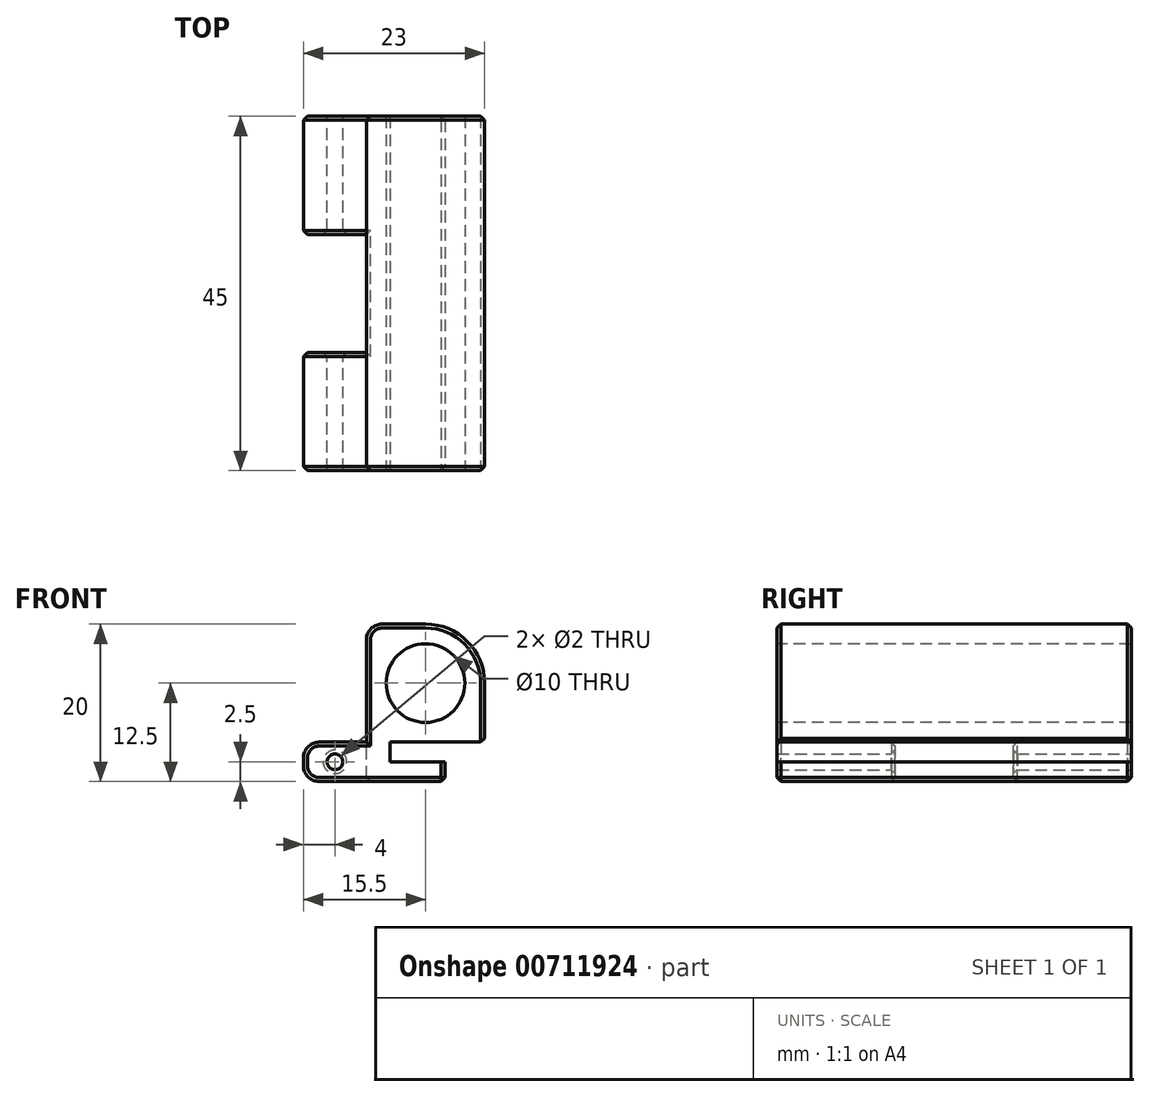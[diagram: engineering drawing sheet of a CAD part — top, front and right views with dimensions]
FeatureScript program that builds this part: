
annotation { "Feature Type Name" : "Feature", "Feature Type Description" : "" }
export const myFeature = defineFeature(function(context is Context, id is Id, definition is map)
    precondition{}
    {
        {
            var Q0;
            Q0=qCreatedBy(makeId("Front.planeOp"),FACE);
            var sketch = newSketch(context, id + "F0", { "sketchPlane" : qUnion([Q0])});
            skLineSegment(sketch, "E0.bottom", {"start": v(0, 0) * mm, "end": v(15, 0) * mm});
            skLineSegment(sketch, "E0.top", {"start": v(0, 15) * mm, "end": v(15, 15) * mm});
            skLineSegment(sketch, "E0.left", {"start": v(0, 0) * mm, "end": v(0, 15) * mm});
            skLineSegment(sketch, "E0.right", {"start": v(15, 0) * mm, "end": v(15, 15) * mm});
            skSolve(sketch);
        }
        {
            var Q0;
            Q0=makeQuery(id+"F0.imprint","IMPRINT",FACE,{"disambiguationData":[TD([[makeQuery(id+"F0.imprint","IMPRINT",EDGE,{"derivedFrom":sQuery(id+"F0.wireOp",EDGE,"E0.bottom")}),1.0]])]});
            extrude(context, id + "F1", {"entities" : qUnion([Q0]), "oppositeDirection" : true, "depth" : 45 * mm, "offsetDistance" : 25 * mm});
        }
        {
            var Q0;
            Q0=makeQuery(id+"F1.opExtrude","CAP_FACE",FACE,{"disambiguationData":[OSD([sQuery(id+"F0.wireOp",EDGE,"E0.bottom"),sQuery(id+"F0.wireOp",EDGE,"E0.top"),sQuery(id+"F0.wireOp",EDGE,"E0.left"),sQuery(id+"F0.wireOp",EDGE,"E0.right")])],"isStart":true});
            var sketch = newSketch(context, id + "F2", { "sketchPlane" : qUnion([Q0])});
            skCircle(sketch, "E1", {"center": v(7.5, 7.5) * mm, "radius": 5 * mm});
            skPoint(sketch, "E1.centerSnap0", {"position": v(15, 7.5) * mm});
            skPoint(sketch, "E1.centerSnap1", {"position": v(7.5, 0) * mm});
            skSolve(sketch);
        }
        {
            var Q0;
            Q0 = qSketchRegion(id + "F2", true);
            extrude(context, id + "F3", {"entities" : qUnion([Q0]), "operationType" : NewBodyOperationType.REMOVE, "oppositeDirection" : true, "depth" : 45 * mm, "offsetDistance" : 25 * mm});
        }
        {
            var Q0;
            Q0=makeQuery(id+"F1.opExtrude","SWEPT_EDGE",EDGE,{"disambiguationData":[OSD([sQuery(id+"F0.wireOp",EDGE,"E0.top"),sQuery(id+"F0.wireOp",EDGE,"E0.right")])]});
            fillet(context, id + "F4", {"entities" : qUnion([Q0]), "tangentPropagation" : true, "radius" : 7.5 * mm, "defaultsChanged" : false, "vertexSettings" : [], "allowEdgeOverflow" : false});
        }
        {
            var Q0;
            Q0=makeQuery(id+"F1.opExtrude","SWEPT_FACE",FACE,{"disambiguationData":[OSD([sQuery(id+"F0.wireOp",EDGE,"E0.left")])]});
            var sketch = newSketch(context, id + "F5", { "sketchPlane" : qUnion([Q0])});
            skSolve(sketch);
        }
        {
            var Q0;
            Q0=makeQuery(id+"F1.opExtrude","CAP_FACE",FACE,{"disambiguationData":[OSD([sQuery(id+"F0.wireOp",EDGE,"E0.bottom"),sQuery(id+"F0.wireOp",EDGE,"E0.top"),sQuery(id+"F0.wireOp",EDGE,"E0.left"),sQuery(id+"F0.wireOp",EDGE,"E0.right")])],"isStart":true});
            var sketch = newSketch(context, id + "F6", { "sketchPlane" : qUnion([Q0])});
            skLineSegment(sketch, "E2.bottom", {"start": v(0, 0) * mm, "end": v(10, 0) * mm});
            skLineSegment(sketch, "E2.top", {"start": v(0, -5) * mm, "end": v(10, -5) * mm});
            skLineSegment(sketch, "E2.left", {"start": v(0, 0) * mm, "end": v(0, -5) * mm});
            skLineSegment(sketch, "E2.right", {"start": v(10, 0) * mm, "end": v(10, -5) * mm});
            skSolve(sketch);
        }
        {
            var Q0;
            Q0 = qSketchRegion(id + "F6", true);
            extrude(context, id + "F7", {"entities" : qUnion([Q0]), "operationType" : NewBodyOperationType.ADD, "oppositeDirection" : true, "depth" : 45 * mm, "offsetDistance" : 25 * mm});
        }
        {
            var Q0;
            Q0=makeQuery(id+"F7.boolean.opBoolean","MERGE",FACE,{"derivedFrom":[makeQuery(id+"F1.opExtrude","CAP_FACE",FACE,{"disambiguationData":[OSD([sQuery(id+"F0.wireOp",EDGE,"E0.bottom"),sQuery(id+"F0.wireOp",EDGE,"E0.top"),sQuery(id+"F0.wireOp",EDGE,"E0.left"),sQuery(id+"F0.wireOp",EDGE,"E0.right")])],"isStart":true}),makeQuery(id+"F7.opExtrude","CAP_FACE",FACE,{"disambiguationData":[OSD([sQuery(id+"F6.wireOp",EDGE,"E2.bottom"),sQuery(id+"F6.wireOp",EDGE,"E2.top"),sQuery(id+"F6.wireOp",EDGE,"E2.left"),sQuery(id+"F6.wireOp",EDGE,"E2.right")])],"isStart":true})]});
            var sketch = newSketch(context, id + "F8", { "sketchPlane" : qUnion([Q0])});
            skPoint(sketch, "E3.oppositeSnap0", {"position": v(10, -2.5) * mm});
            skLineSegment(sketch, "E3.bottom", {"start": v(10, 0) * mm, "end": v(3, 0) * mm});
            skLineSegment(sketch, "E3.top", {"start": v(10, -2.5) * mm, "end": v(3, -2.5) * mm});
            skLineSegment(sketch, "E3.left", {"start": v(10, 0) * mm, "end": v(10, -2.5) * mm});
            skLineSegment(sketch, "E3.right", {"start": v(3, 0) * mm, "end": v(3, -2.5) * mm});
            skSolve(sketch);
        }
        {
            var Q0;
            Q0 = qSketchRegion(id + "F8", true);
            extrude(context, id + "F9", {"entities" : qUnion([Q0]), "operationType" : NewBodyOperationType.REMOVE, "oppositeDirection" : true, "depth" : 45 * mm, "offsetDistance" : 25 * mm});
        }
        {
            var Q0;
            {var subQ0=sQuery(id+"F0.wireOp",EDGE,"E0.left");Q0=makeQuery(id+"F5.imprint","IMPRINT",FACE,{"disambiguationData":[TD([[makeQuery(id+"F5.imprint","IMPRINT",EDGE,{"derivedFrom":makeQuery(id+"F1.opExtrude","CAP_EDGE",EDGE,{"disambiguationData":[OSD([subQ0])],"isStart":true})}),1.0]])]});}
            var sketch = newSketch(context, id + "F10", { "sketchPlane" : qUnion([Q0])});
            skLineSegment(sketch, "E4.bottom", {"start": v(0, 0) * mm, "end": v(-15, 0) * mm});
            skLineSegment(sketch, "E4.top", {"start": v(0, -5) * mm, "end": v(-15, -5) * mm});
            skLineSegment(sketch, "E4.left", {"start": v(0, 0) * mm, "end": v(0, -5) * mm});
            skLineSegment(sketch, "E4.right", {"start": v(-15, 0) * mm, "end": v(-15, -5) * mm});
            skSolve(sketch);
        }
        {
            var Q0;
            Q0 = qSketchRegion(id + "F10", true);
            extrude(context, id + "F11", {"entities" : qUnion([Q0]), "operationType" : NewBodyOperationType.ADD, "depth" : 8 * mm, "offsetDistance" : 25 * mm});
        }
        {
            var Q0;
            Q0=makeQuery(id+"F7.boolean.opBoolean","MERGE",FACE,{"derivedFrom":[makeQuery(id+"F1.opExtrude","SWEPT_FACE",FACE,{"disambiguationData":[OSD([sQuery(id+"F0.wireOp",EDGE,"E0.left")])]}),makeQuery(id+"F7.opExtrude","SWEPT_FACE",FACE,{"disambiguationData":[OSD([sQuery(id+"F6.wireOp",EDGE,"E2.left")])]})]});
            var sketch = newSketch(context, id + "F12", { "sketchPlane" : qUnion([Q0])});
            skLineSegment(sketch, "E5.bottom", {"start": v(-45, -5) * mm, "end": v(-30, -5) * mm});
            skLineSegment(sketch, "E5.top", {"start": v(-45, 0) * mm, "end": v(-30, 0) * mm});
            skLineSegment(sketch, "E5.left", {"start": v(-45, -5) * mm, "end": v(-45, 0) * mm});
            skLineSegment(sketch, "E5.right", {"start": v(-30, -5) * mm, "end": v(-30, 0) * mm});
            skSolve(sketch);
        }
        {
            var Q0;
            Q0 = qSketchRegion(id + "F12", true);
            extrude(context, id + "F13", {"entities" : qUnion([Q0]), "operationType" : NewBodyOperationType.ADD, "depth" : 8 * mm, "offsetDistance" : 25 * mm});
        }
        {
            var Q0;
            Q0=makeQuery(id+"F13.boolean.opBoolean","MERGE",FACE,{"derivedFrom":[makeQuery(id+"F7.boolean.opBoolean","MERGE",FACE,{"derivedFrom":[makeQuery(id+"F1.opExtrude","CAP_FACE",FACE,{"disambiguationData":[OSD([sQuery(id+"F0.wireOp",EDGE,"E0.bottom"),sQuery(id+"F0.wireOp",EDGE,"E0.top"),sQuery(id+"F0.wireOp",EDGE,"E0.left"),sQuery(id+"F0.wireOp",EDGE,"E0.right")])],"isStart":false}),makeQuery(id+"F7.opExtrude","CAP_FACE",FACE,{"disambiguationData":[OSD([sQuery(id+"F6.wireOp",EDGE,"E2.bottom"),sQuery(id+"F6.wireOp",EDGE,"E2.top"),sQuery(id+"F6.wireOp",EDGE,"E2.left"),sQuery(id+"F6.wireOp",EDGE,"E2.right")])],"isStart":false})]}),makeQuery(id+"F13.opExtrude","SWEPT_FACE",FACE,{"disambiguationData":[OSD([sQuery(id+"F12.wireOp",EDGE,"E5.left")])]})]});
            var sketch = newSketch(context, id + "F14", { "sketchPlane" : qUnion([Q0])});
            skCircle(sketch, "E6", {"center": v(4, -2.5) * mm, "radius": 1 * mm});
            skPoint(sketch, "E6.centerSnap0", {"position": v(4, 0) * mm});
            skPoint(sketch, "E6.centerSnap1", {"position": v(8, -2.5) * mm});
            skSolve(sketch);
        }
        {
            var Q0;
            Q0 = qSketchRegion(id + "F14", true);
            extrude(context, id + "F15", {"entities" : qUnion([Q0]), "operationType" : NewBodyOperationType.REMOVE, "oppositeDirection" : true, "depth" : 45 * mm, "offsetDistance" : 25 * mm});
        }
        {
            var Q0;
            Q0=makeQuery(id+"F13.opExtrude","CAP_EDGE",EDGE,{"disambiguationData":[OSD([sQuery(id+"F12.wireOp",EDGE,"E5.top")])],"isStart":false});
            var Q1;
            Q1=makeQuery(id+"F13.opExtrude","CAP_EDGE",EDGE,{"disambiguationData":[OSD([sQuery(id+"F12.wireOp",EDGE,"E5.bottom")])],"isStart":false});
            var Q2;
            Q2=makeQuery(id+"F11.opExtrude","CAP_EDGE",EDGE,{"disambiguationData":[OSD([sQuery(id+"F10.wireOp",EDGE,"E4.top")])],"isStart":false});
            var Q3;
            Q3=makeQuery(id+"F11.opExtrude","CAP_EDGE",EDGE,{"disambiguationData":[OSD([sQuery(id+"F10.wireOp",EDGE,"E4.bottom")])],"isStart":false});
            var Q4;
            Q4=makeQuery(id+"F1.opExtrude","SWEPT_EDGE",EDGE,{"disambiguationData":[OSD([sQuery(id+"F0.wireOp",EDGE,"E0.top"),sQuery(id+"F0.wireOp",EDGE,"E0.left")])]});
            fillet(context, id + "F16", {"entities" : qUnion([Q0, Q1, Q2, Q3, Q4]), "tangentPropagation" : true, "radius" : 2 * mm, "defaultsChanged" : false, "vertexSettings" : [], "allowEdgeOverflow" : false});
        }
        {
            var Q0;
            Q0=makeQuery(id+"F7.boolean.opBoolean","MERGE",EDGE,{"derivedFrom":[makeQuery(id+"F1.opExtrude","CAP_EDGE",EDGE,{"disambiguationData":[OSD([sQuery(id+"F0.wireOp",EDGE,"E0.left")])],"isStart":true}),makeQuery(id+"F7.opExtrude","CAP_EDGE",EDGE,{"disambiguationData":[OSD([sQuery(id+"F6.wireOp",EDGE,"E2.left")])],"isStart":true})]});
            var Q1;
            Q1=makeQuery(id+"F11.opExtrude","SWEPT_EDGE",EDGE,{"disambiguationData":[OSD([sQuery(id+"F0.wireOp",EDGE,"E0.left"),sQuery(id+"F10.wireOp",EDGE,"E4.bottom"),sQuery(id+"F10.wireOp",EDGE,"E4.left")])]});
            var Q2;
            Q2=makeQuery(id+"F7.opExtrude","CAP_EDGE",EDGE,{"disambiguationData":[OSD([sQuery(id+"F6.wireOp",EDGE,"E2.right")])],"isStart":true});
            var Q3;
            Q3=makeQuery(id+"F9.boolean.opBoolean","COPY",EDGE,{"derivedFrom":makeQuery(id+"F9.opExtrude","CAP_EDGE",EDGE,{"disambiguationData":[OSD([sQuery(id+"F8.wireOp",EDGE,"E3.top")])],"isStart":true})});
            var Q4;
            Q4=makeQuery(id+"F9.boolean.opBoolean","COPY",EDGE,{"derivedFrom":makeQuery(id+"F9.opExtrude","CAP_EDGE",EDGE,{"disambiguationData":[OSD([sQuery(id+"F8.wireOp",EDGE,"E3.right")])],"isStart":true})});
            var Q5;
            Q5=makeQuery(id+"F9.boolean.opBoolean","MERGE",EDGE,{"derivedFrom":[makeQuery(id+"F1.opExtrude","CAP_EDGE",EDGE,{"disambiguationData":[OSD([sQuery(id+"F0.wireOp",EDGE,"E0.bottom")])],"isStart":true})],"fromTools":[makeQuery(id+"F9.opExtrude","CAP_EDGE",EDGE,{"disambiguationData":[OSD([sQuery(id+"F8.wireOp",EDGE,"E3.bottom")])],"isStart":true})]});
            var Q6;
            Q6=makeQuery(id+"F3.boolean.opBoolean","COPY",EDGE,{"derivedFrom":makeQuery(id+"F3.opExtrude","CAP_EDGE",EDGE,{"disambiguationData":[OSD([sQuery(id+"F2.wireOp",EDGE,"E1")])],"isStart":true})});
            var Q7;
            Q7=makeQuery(id+"F11.opExtrude","SWEPT_EDGE",EDGE,{"disambiguationData":[OSD([sQuery(id+"F10.wireOp",EDGE,"E4.top"),sQuery(id+"F10.wireOp",EDGE,"E4.right")])]});
            var Q8;
            Q8=makeQuery(id+"F15.boolean.opBoolean","INTERSECT",EDGE,{"derivedFrom":[makeQuery(id+"F11.opExtrude","SWEPT_FACE",FACE,{"disambiguationData":[OSD([sQuery(id+"F10.wireOp",EDGE,"E4.right")])]}),makeQuery(id+"F15.opExtrude","SWEPT_FACE",FACE,{"disambiguationData":[OSD([sQuery(id+"F14.wireOp",EDGE,"E6")])]})]});
            var Q9;
            Q9=makeQuery(id+"F15.boolean.opBoolean","COPY",EDGE,{"derivedFrom":makeQuery(id+"F15.opExtrude","CAP_EDGE",EDGE,{"disambiguationData":[OSD([sQuery(id+"F14.wireOp",EDGE,"E6")])],"isStart":false})});
            var Q10;
            Q10=makeQuery(id+"F15.boolean.opBoolean","INTERSECT",EDGE,{"derivedFrom":[makeQuery(id+"F13.opExtrude","SWEPT_FACE",FACE,{"disambiguationData":[OSD([sQuery(id+"F12.wireOp",EDGE,"E5.right")])]}),makeQuery(id+"F15.opExtrude","SWEPT_FACE",FACE,{"disambiguationData":[OSD([sQuery(id+"F14.wireOp",EDGE,"E6")])]})]});
            var Q11;
            Q11=makeQuery(id+"F13.opExtrude","SWEPT_EDGE",EDGE,{"disambiguationData":[OSD([sQuery(id+"F6.wireOp",EDGE,"E2.top"),sQuery(id+"F6.wireOp",EDGE,"E2.left"),sQuery(id+"F12.wireOp",EDGE,"E5.bottom"),sQuery(id+"F12.wireOp",EDGE,"E5.right")])]});
            var Q12;
            Q12=makeQuery(id+"F16.opFillet","BLEND_EDGE",EDGE,{"blendedFrom":[makeQuery(id+"F13.opExtrude","CAP_EDGE",EDGE,{"disambiguationData":[OSD([sQuery(id+"F12.wireOp",EDGE,"E5.bottom")])],"isStart":false}),makeQuery(id+"F13.boolean.opBoolean","MERGE",FACE,{"derivedFrom":[makeQuery(id+"F7.boolean.opBoolean","MERGE",FACE,{"derivedFrom":[makeQuery(id+"F1.opExtrude","CAP_FACE",FACE,{"disambiguationData":[OSD([sQuery(id+"F0.wireOp",EDGE,"E0.bottom"),sQuery(id+"F0.wireOp",EDGE,"E0.top"),sQuery(id+"F0.wireOp",EDGE,"E0.left"),sQuery(id+"F0.wireOp",EDGE,"E0.right")])],"isStart":false}),makeQuery(id+"F7.opExtrude","CAP_FACE",FACE,{"disambiguationData":[OSD([sQuery(id+"F6.wireOp",EDGE,"E2.bottom"),sQuery(id+"F6.wireOp",EDGE,"E2.top"),sQuery(id+"F6.wireOp",EDGE,"E2.left"),sQuery(id+"F6.wireOp",EDGE,"E2.right")])],"isStart":false})]}),makeQuery(id+"F13.opExtrude","SWEPT_FACE",FACE,{"disambiguationData":[OSD([sQuery(id+"F12.wireOp",EDGE,"E5.left")])]})]})],"blendedInto":[makeQuery(id+"F13.boolean.opBoolean","MERGE",FACE,{"derivedFrom":[makeQuery(id+"F7.boolean.opBoolean","MERGE",FACE,{"derivedFrom":[makeQuery(id+"F1.opExtrude","CAP_FACE",FACE,{"disambiguationData":[OSD([sQuery(id+"F0.wireOp",EDGE,"E0.bottom"),sQuery(id+"F0.wireOp",EDGE,"E0.top"),sQuery(id+"F0.wireOp",EDGE,"E0.left"),sQuery(id+"F0.wireOp",EDGE,"E0.right")])],"isStart":false}),makeQuery(id+"F7.opExtrude","CAP_FACE",FACE,{"disambiguationData":[OSD([sQuery(id+"F6.wireOp",EDGE,"E2.bottom"),sQuery(id+"F6.wireOp",EDGE,"E2.top"),sQuery(id+"F6.wireOp",EDGE,"E2.left"),sQuery(id+"F6.wireOp",EDGE,"E2.right")])],"isStart":false})]}),makeQuery(id+"F13.opExtrude","SWEPT_FACE",FACE,{"disambiguationData":[OSD([sQuery(id+"F12.wireOp",EDGE,"E5.left")])]})]})]});
            var Q13;
            Q13=makeQuery(id+"F7.opExtrude","CAP_EDGE",EDGE,{"disambiguationData":[OSD([sQuery(id+"F6.wireOp",EDGE,"E2.right")])],"isStart":false});
            var Q14;
            Q14=makeQuery(id+"F9.boolean.opBoolean","COPY",EDGE,{"derivedFrom":makeQuery(id+"F9.opExtrude","CAP_EDGE",EDGE,{"disambiguationData":[OSD([sQuery(id+"F8.wireOp",EDGE,"E3.top")])],"isStart":false})});
            var Q15;
            Q15=makeQuery(id+"F9.boolean.opBoolean","COPY",EDGE,{"derivedFrom":makeQuery(id+"F9.opExtrude","CAP_EDGE",EDGE,{"disambiguationData":[OSD([sQuery(id+"F8.wireOp",EDGE,"E3.right")])],"isStart":false})});
            var Q16;
            Q16=makeQuery(id+"F9.boolean.opBoolean","MERGE",EDGE,{"derivedFrom":[makeQuery(id+"F1.opExtrude","CAP_EDGE",EDGE,{"disambiguationData":[OSD([sQuery(id+"F0.wireOp",EDGE,"E0.bottom")])],"isStart":false})],"fromTools":[makeQuery(id+"F9.opExtrude","CAP_EDGE",EDGE,{"disambiguationData":[OSD([sQuery(id+"F8.wireOp",EDGE,"E3.bottom")])],"isStart":false})]});
            var Q17;
            Q17=makeQuery(id+"F3.boolean.opBoolean","COPY",EDGE,{"derivedFrom":makeQuery(id+"F3.opExtrude","CAP_EDGE",EDGE,{"disambiguationData":[OSD([sQuery(id+"F2.wireOp",EDGE,"E1")])],"isStart":false})});
            var Q18;
            Q18=makeQuery(id+"F1.opExtrude","CAP_EDGE",EDGE,{"disambiguationData":[OSD([sQuery(id+"F0.wireOp",EDGE,"E0.right")])],"isStart":false});
            var Q19;
            Q19=makeQuery(id+"F15.boolean.opBoolean","COPY",EDGE,{"derivedFrom":makeQuery(id+"F15.opExtrude","CAP_EDGE",EDGE,{"disambiguationData":[OSD([sQuery(id+"F14.wireOp",EDGE,"E6")])],"isStart":true})});
            var Q20;
            Q20=makeQuery(id+"F1.opExtrude","SWEPT_EDGE",EDGE,{"disambiguationData":[OSD([sQuery(id+"F0.wireOp",EDGE,"E0.bottom"),sQuery(id+"F0.wireOp",EDGE,"E0.right")])]});
            var Q21;
            Q21=makeQuery(id+"F7.opExtrude","SWEPT_EDGE",EDGE,{"disambiguationData":[OSD([sQuery(id+"F6.wireOp",EDGE,"E2.top"),sQuery(id+"F6.wireOp",EDGE,"E2.right")])]});
            var Q22;
            Q22=makeQuery(id+"F9.boolean.opBoolean","COPY",EDGE,{"derivedFrom":makeQuery(id+"F9.opExtrude","SWEPT_EDGE",EDGE,{"disambiguationData":[OSD([sQuery(id+"F6.wireOp",EDGE,"E2.right"),sQuery(id+"F8.wireOp",EDGE,"E3.top"),sQuery(id+"F8.wireOp",EDGE,"E3.left")])]})});
            var Q23;
            Q23=makeQuery(id+"F7.opExtrude","SWEPT_EDGE",EDGE,{"disambiguationData":[OSD([sQuery(id+"F6.wireOp",EDGE,"E2.top"),sQuery(id+"F6.wireOp",EDGE,"E2.left")])]});
            chamfer(context, id + "F17", {"entities" : qUnion([Q0, Q1, Q2, Q3, Q4, Q5, Q6, Q7, Q8, Q9, Q10, Q11, Q12, Q13, Q14, Q15, Q16, Q17, Q18, Q19, Q20, Q21, Q22, Q23]), "width" : 0.5 * mm, "tangentPropagation" : true});
        }
    });
